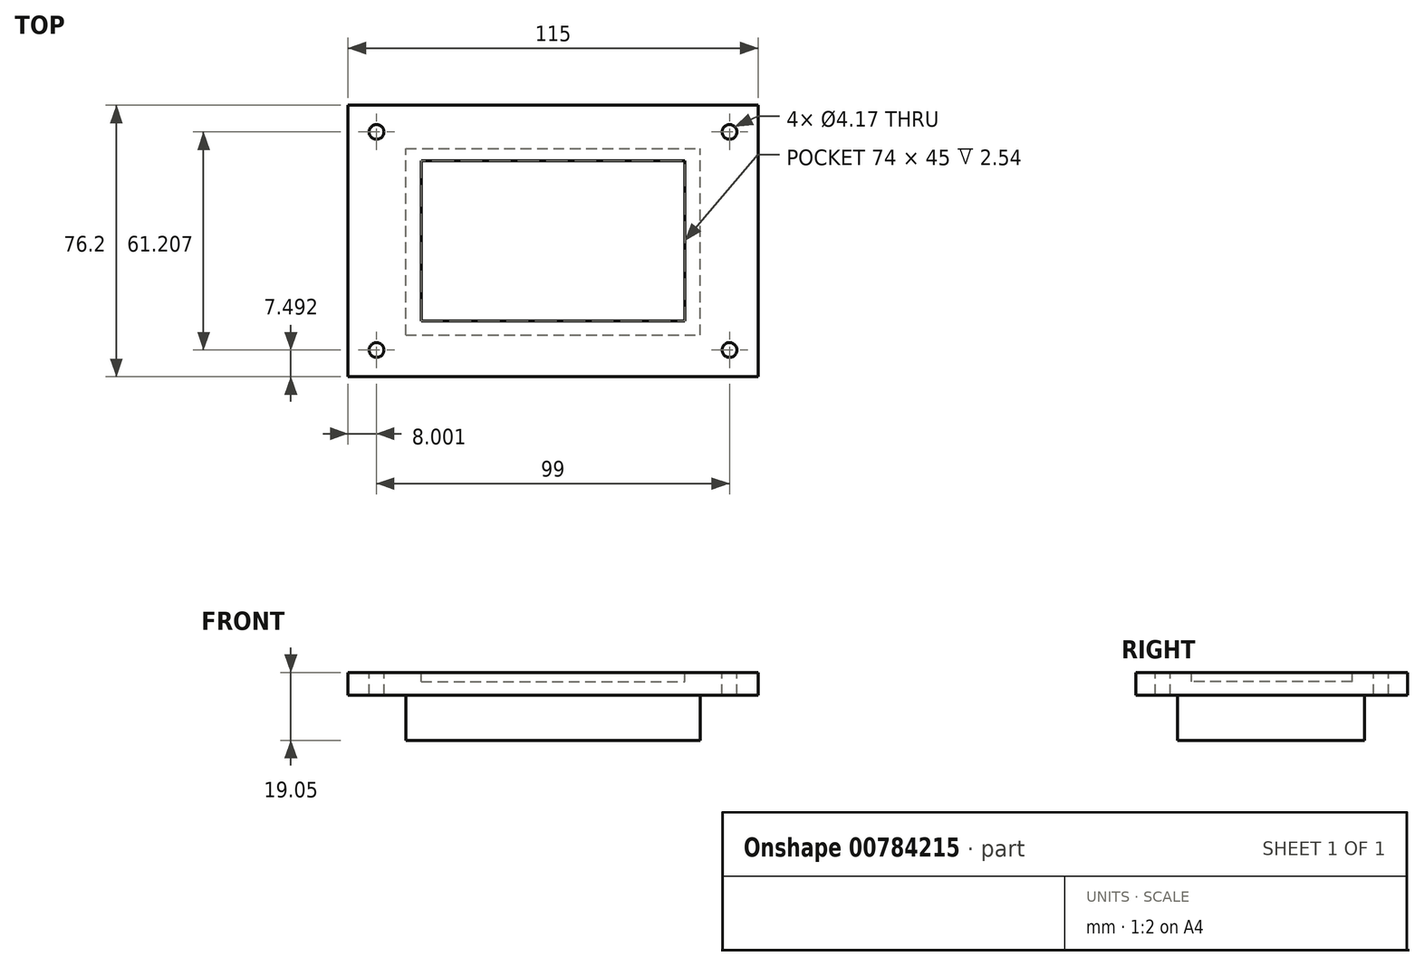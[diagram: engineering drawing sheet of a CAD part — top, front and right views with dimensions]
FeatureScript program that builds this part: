
annotation { "Feature Type Name" : "Feature", "Feature Type Description" : "" }
export const myFeature = defineFeature(function(context is Context, id is Id, definition is map)
    precondition{}
    {
        {
            var Q0;
            Q0=qCreatedBy(makeId("Top.planeOp"),FACE);
            var sketch = newSketch(context, id + "F0", { "sketchPlane" : qUnion([Q0])});
            skLineSegment(sketch, "E0.bottom", {"start": v(-53.27, 41.04) * mm, "end": v(61.73, 41.04) * mm});
            skLineSegment(sketch, "E0.top", {"start": v(-53.27, -35.16) * mm, "end": v(61.73, -35.16) * mm});
            skLineSegment(sketch, "E0.left", {"start": v(-53.27, 41.04) * mm, "end": v(-53.27, -35.16) * mm});
            skLineSegment(sketch, "E0.right", {"start": v(61.73, 41.04) * mm, "end": v(61.73, -35.16) * mm});
            skSolve(sketch);
        }
        {
            var Q0;
            Q0=makeQuery(id+"F0.imprint","IMPRINT",FACE,{"disambiguationData":[TD([[makeQuery(id+"F0.imprint","IMPRINT",EDGE,{"derivedFrom":sQuery(id+"F0.wireOp",EDGE,"E0.bottom")}),-1.0]])]});
            extrude(context, id + "F1", {"entities" : qUnion([Q0]), "depth" : 6.35 * mm, "offsetDistance" : 25.4 * mm});
        }
        {
            var Q0;
            Q0=makeQuery(id+"F1.opExtrude","CAP_FACE",FACE,{"disambiguationData":[OSD([sQuery(id+"F0.wireOp",EDGE,"E0.bottom"),sQuery(id+"F0.wireOp",EDGE,"E0.top"),sQuery(id+"F0.wireOp",EDGE,"E0.left"),sQuery(id+"F0.wireOp",EDGE,"E0.right")])],"isStart":true});
            var sketch = newSketch(context, id + "F2", { "sketchPlane" : qUnion([Q0])});
            skLineSegment(sketch, "E1.bottom", {"start": v(-37.05, 23.48) * mm, "end": v(45.5, 23.48) * mm});
            skLineSegment(sketch, "E1.top", {"start": v(-37.05, -28.91) * mm, "end": v(45.5, -28.91) * mm});
            skLineSegment(sketch, "E1.left", {"start": v(-37.05, 23.48) * mm, "end": v(-37.05, -28.91) * mm});
            skLineSegment(sketch, "E1.right", {"start": v(45.5, 23.48) * mm, "end": v(45.5, -28.91) * mm});
            skSolve(sketch);
        }
        {
            var Q0;
            Q0=makeQuery(id+"F2.imprint","IMPRINT",FACE,{"disambiguationData":[TD([[makeQuery(id+"F2.imprint","IMPRINT",EDGE,{"derivedFrom":sQuery(id+"F2.wireOp",EDGE,"E1.bottom")}),-1.0]])]});
            extrude(context, id + "F3", {"entities" : qUnion([Q0]), "operationType" : NewBodyOperationType.ADD, "depth" : 12.7 * mm, "offsetDistance" : 25.4 * mm});
        }
        {
            var Q0;
            Q0=makeQuery(id+"F1.opExtrude","CAP_FACE",FACE,{"disambiguationData":[OSD([sQuery(id+"F0.wireOp",EDGE,"E0.bottom"),sQuery(id+"F0.wireOp",EDGE,"E0.top"),sQuery(id+"F0.wireOp",EDGE,"E0.left"),sQuery(id+"F0.wireOp",EDGE,"E0.right")])],"isStart":false});
            var sketch = newSketch(context, id + "F4", { "sketchPlane" : qUnion([Q0])});
            skLineSegment(sketch, "E2.bottom", {"start": v(-32.77, 25.44) * mm, "end": v(41.23, 25.44) * mm});
            skLineSegment(sketch, "E2.top", {"start": v(-32.77, -19.56) * mm, "end": v(41.23, -19.56) * mm});
            skLineSegment(sketch, "E2.left", {"start": v(-32.77, 25.44) * mm, "end": v(-32.77, -19.56) * mm});
            skLineSegment(sketch, "E2.right", {"start": v(41.23, 25.44) * mm, "end": v(41.23, -19.56) * mm});
            skSolve(sketch);
        }
        {
            var Q0;
            Q0=makeQuery(id+"F4.imprint","IMPRINT",FACE,{"disambiguationData":[TD([[makeQuery(id+"F4.imprint","IMPRINT",EDGE,{"derivedFrom":sQuery(id+"F4.wireOp",EDGE,"E2.bottom")}),-1.0]])]});
            extrude(context, id + "F5", {"entities" : qUnion([Q0]), "operationType" : NewBodyOperationType.REMOVE, "oppositeDirection" : true, "depth" : 2.54 * mm, "offsetDistance" : 25.4 * mm});
        }
        {
            var Q0;
            Q0=makeQuery(id+"F1.opExtrude","CAP_FACE",FACE,{"disambiguationData":[OSD([sQuery(id+"F0.wireOp",EDGE,"E0.bottom"),sQuery(id+"F0.wireOp",EDGE,"E0.top"),sQuery(id+"F0.wireOp",EDGE,"E0.left"),sQuery(id+"F0.wireOp",EDGE,"E0.right")])],"isStart":false});
            var sketch = newSketch(context, id + "F6", { "sketchPlane" : qUnion([Q0])});
            skPoint(sketch, "E3", {"position": v(-45.27, 33.54) * mm});
            skPoint(sketch, "E4", {"position": v(53.73, 33.54) * mm});
            skPoint(sketch, "E5", {"position": v(53.73, -27.67) * mm});
            skPoint(sketch, "E6", {"position": v(-45.27, -27.67) * mm});
            skLineSegment(sketch, "E7.bottom", {"start": v(-37.85, 30.52) * mm, "end": v(46.3, 30.52) * mm});
            skLineSegment(sketch, "E7.top", {"start": v(-37.85, -24.64) * mm, "end": v(46.3, -24.64) * mm});
            skLineSegment(sketch, "E7.left", {"start": v(-37.85, 30.52) * mm, "end": v(-37.85, -24.64) * mm});
            skLineSegment(sketch, "E7.right", {"start": v(46.3, 30.52) * mm, "end": v(46.3, -24.64) * mm});
            skSolve(sketch);
        }
        {
            var Q0;
            Q0=sQuery(id+"F6.wireOp",VERTEX,"E3");
            var Q1;
            Q1=sQuery(id+"F6.wireOp",VERTEX,"E4");
            var Q2;
            Q2=sQuery(id+"F6.wireOp",VERTEX,"E5");
            var Q3;
            Q3=sQuery(id+"F6.wireOp",VERTEX,"E6");
            var Q4;
            Q4=makeQuery(id+"F1.opExtrude","SWEPT_BODY",BODY,{"disambiguationData":[OSD([sQuery(id+"F0.wireOp",EDGE,"E0.bottom"),sQuery(id+"F0.wireOp",EDGE,"E0.top"),sQuery(id+"F0.wireOp",EDGE,"E0.left"),sQuery(id+"F0.wireOp",EDGE,"E0.right")])]});
            hole(context, id + "F7", {"style" : HoleStyle.SIMPLE, "endStyle" : HoleEndStyle.THROUGH, "holeDiameter" : 4.17 * mm, "majorDiameter" : 6.35 * mm, "isTappedThrough" : true, "tappedDepth" : 12.7 * mm, "tapClearance" : 3, "locations" : qUnion([Q0, Q1, Q2, Q3]), "scope" : qUnion([Q4])});
        }
    });
